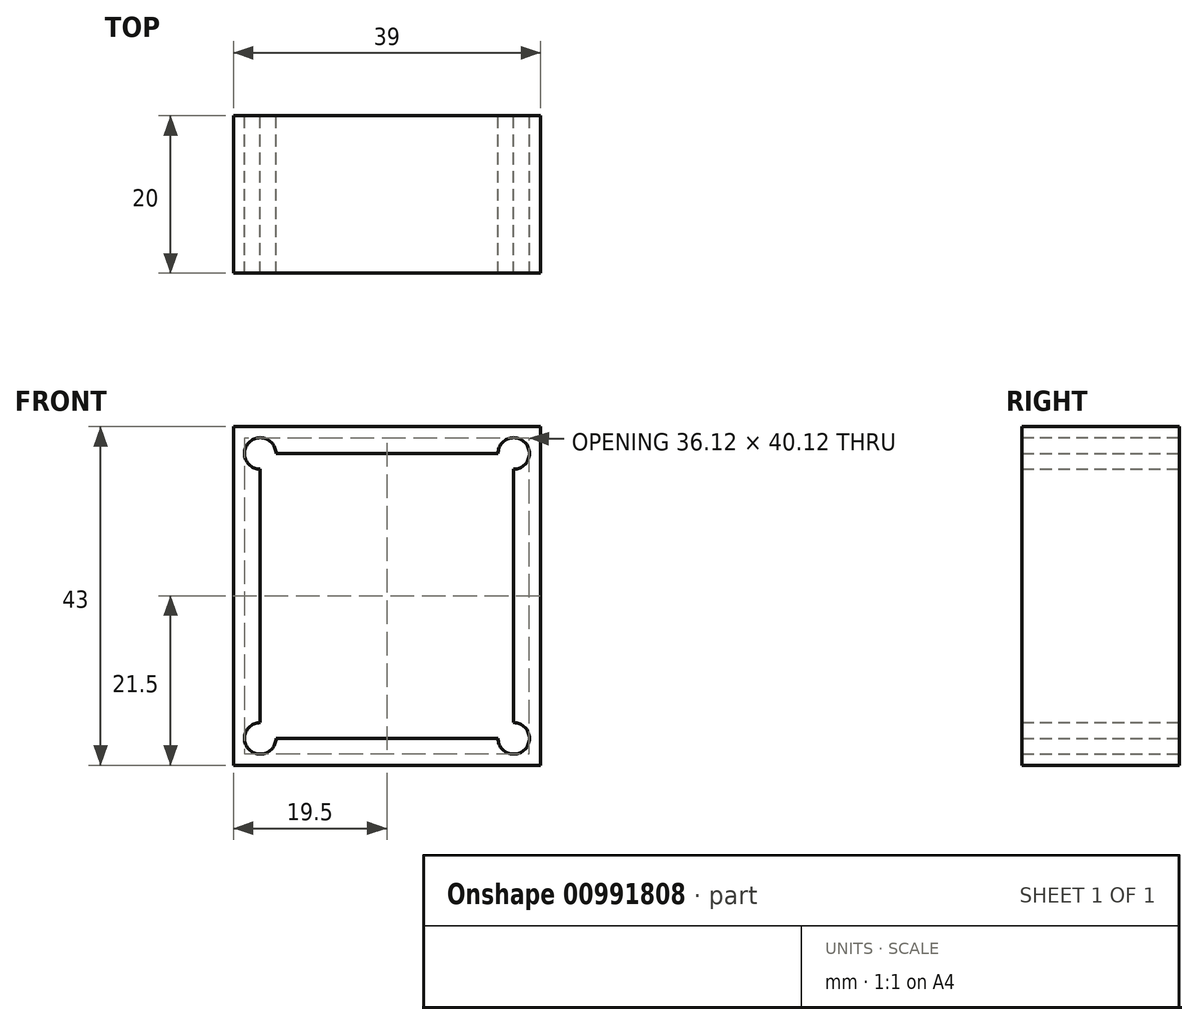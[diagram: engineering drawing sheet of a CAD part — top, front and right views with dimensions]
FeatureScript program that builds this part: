
annotation { "Feature Type Name" : "Feature", "Feature Type Description" : "" }
export const myFeature = defineFeature(function(context is Context, id is Id, definition is map)
    precondition{}
    {
        {
            var Q0;
            Q0=qCreatedBy(makeId("Front.planeOp"),FACE);
            var sketch = newSketch(context, id + "F0", { "sketchPlane" : qUnion([Q0])});
            skLineSegment(sketch, "E0.bottom", {"start": v(14.1, 18.1) * mm, "end": v(-14.1, 18.1) * mm});
            skLineSegment(sketch, "E0.top", {"start": v(14.1, -18.1) * mm, "end": v(-14.1, -18.1) * mm});
            skLineSegment(sketch, "E0.left", {"start": v(16.1, 16.1) * mm, "end": v(16.1, -16.1) * mm});
            skLineSegment(sketch, "E0.right", {"start": v(-16.1, 16.1) * mm, "end": v(-16.1, -16.1) * mm});
            skPoint(sketch, "E0.middle", {"position": v(0, 0) * mm});
            skCircle(sketch, "E1", {"center": v(0, 0) * mm, "radius": 6 * mm});
            skLineSegment(sketch, "E2", {"start": v(1.1, -15.1) * mm, "end": v(-11.1, -15.1) * mm});
            skLineSegment(sketch, "E3", {"start": v(3.1, -17.1) * mm, "end": v(3.1, -18.1) * mm});
            skLineSegment(sketch, "E4", {"start": v(13.1, -10.8) * mm, "end": v(13.1, 13.1) * mm});
            skLineSegment(sketch, "E5", {"start": v(15.1, -12.8) * mm, "end": v(16.1, -12.8) * mm});
            skLineSegment(sketch, "E6", {"start": v(-13.1, 9.02) * mm, "end": v(-13.1, -13.1) * mm});
            skLineSegment(sketch, "E7", {"start": v(-15.1, 11.02) * mm, "end": v(-16.1, 11.02) * mm});
            skLineSegment(sketch, "E8", {"start": v(-9.1, 15.1) * mm, "end": v(11.1, 15.1) * mm});
            skLineSegment(sketch, "E9", {"start": v(-11.1, 17.1) * mm, "end": v(-11.1, 18.1) * mm});
            skPoint(sketch, "E10.visualSharp", {"position": v(-13.1, -15.1) * mm});
            skArc(sketch, "E10.filletArc", {"start": v(-13.1, -13.1) * mm, "mid": v(-12.51, -14.51) * mm, "end": v(-11.1, -15.1) * mm});
            skPoint(sketch, "E11.visualSharp", {"position": v(13.1, 15.1) * mm});
            skArc(sketch, "E11.filletArc", {"start": v(13.1, 13.1) * mm, "mid": v(12.51, 14.51) * mm, "end": v(11.1, 15.1) * mm});
            skPoint(sketch, "E12.visualSharp", {"position": v(-11.1, 15.1) * mm});
            skArc(sketch, "E12.filletArc", {"start": v(-11.1, 17.1) * mm, "mid": v(-10.51, 15.69) * mm, "end": v(-9.1, 15.1) * mm});
            skPoint(sketch, "E13.visualSharp", {"position": v(-13.1, 11.02) * mm});
            skArc(sketch, "E13.filletArc", {"start": v(-13.1, 9.02) * mm, "mid": v(-13.69, 10.43) * mm, "end": v(-15.1, 11.02) * mm});
            skPoint(sketch, "E14.visualSharp", {"position": v(3.1, -15.1) * mm});
            skArc(sketch, "E14.filletArc", {"start": v(3.1, -17.1) * mm, "mid": v(2.51, -15.69) * mm, "end": v(1.1, -15.1) * mm});
            skPoint(sketch, "E15.visualSharp", {"position": v(13.1, -12.8) * mm});
            skArc(sketch, "E15.filletArc", {"start": v(13.1, -10.8) * mm, "mid": v(13.69, -12.21) * mm, "end": v(15.1, -12.8) * mm});
            skArc(sketch, "E16", {"start": v(-14.1, 18.1) * mm, "mid": v(-17.51, 19.51) * mm, "end": v(-16.1, 16.1) * mm});
            skArc(sketch, "E17", {"start": v(16.1, 16.1) * mm, "mid": v(17.51, 19.51) * mm, "end": v(14.1, 18.1) * mm});
            skArc(sketch, "E18", {"start": v(-16.1, -16.1) * mm, "mid": v(-17.51, -19.51) * mm, "end": v(-14.1, -18.1) * mm});
            skArc(sketch, "E19", {"start": v(14.1, -18.1) * mm, "mid": v(17.51, -19.51) * mm, "end": v(16.1, -16.1) * mm});
            skLineSegment(sketch, "E20.bottom", {"start": v(19.5, 21.5) * mm, "end": v(-19.5, 21.5) * mm});
            skLineSegment(sketch, "E20.top", {"start": v(19.5, -21.5) * mm, "end": v(-19.5, -21.5) * mm});
            skLineSegment(sketch, "E20.left", {"start": v(19.5, 21.5) * mm, "end": v(19.5, -21.5) * mm});
            skLineSegment(sketch, "E20.right", {"start": v(-19.5, 21.5) * mm, "end": v(-19.5, -21.5) * mm});
            skSolve(sketch);
        }
        {
            var Q0;
            {var subQ3=sQuery(id+"F0.wireOp",EDGE,"E16");Q0=makeQuery(id+"F0.imprint","IMPRINT",FACE,{"disambiguationData":[TD([[makeQuery(id+"F0.imprint","IMPRINT",EDGE,{"derivedFrom":subQ3}),-1.0]])]});}
            extrude(context, id + "F1", {"entities" : qUnion([Q0]), "depth" : 20 * mm, "offsetDistance" : 25 * mm});
        }
    });
